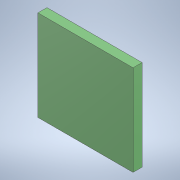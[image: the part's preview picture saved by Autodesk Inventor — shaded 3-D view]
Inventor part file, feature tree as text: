
AUTODESK INVENTOR PART (.ipt)
format: ipt  version: 2021 (Build 250183000, 183)  size: 95,744 bytes
history: native  units: mm
features: other x1, extrude x1, sketch x1
ambient origin geometry x8: Origin, YZ Plane, XZ Plane, XY Plane, X Axis, Y Axis, Z Axis, Center Point
bodies: Body1 (feature_tree)
feature tree (3):
  other  "Sólido1"
  extrude  "Extrusão1"  Depth=210.0mm
  sketch  "Esboço1"  dims[d0=200.0mm d1=210.0mm d2=20.0mm d3=0.0mm]
